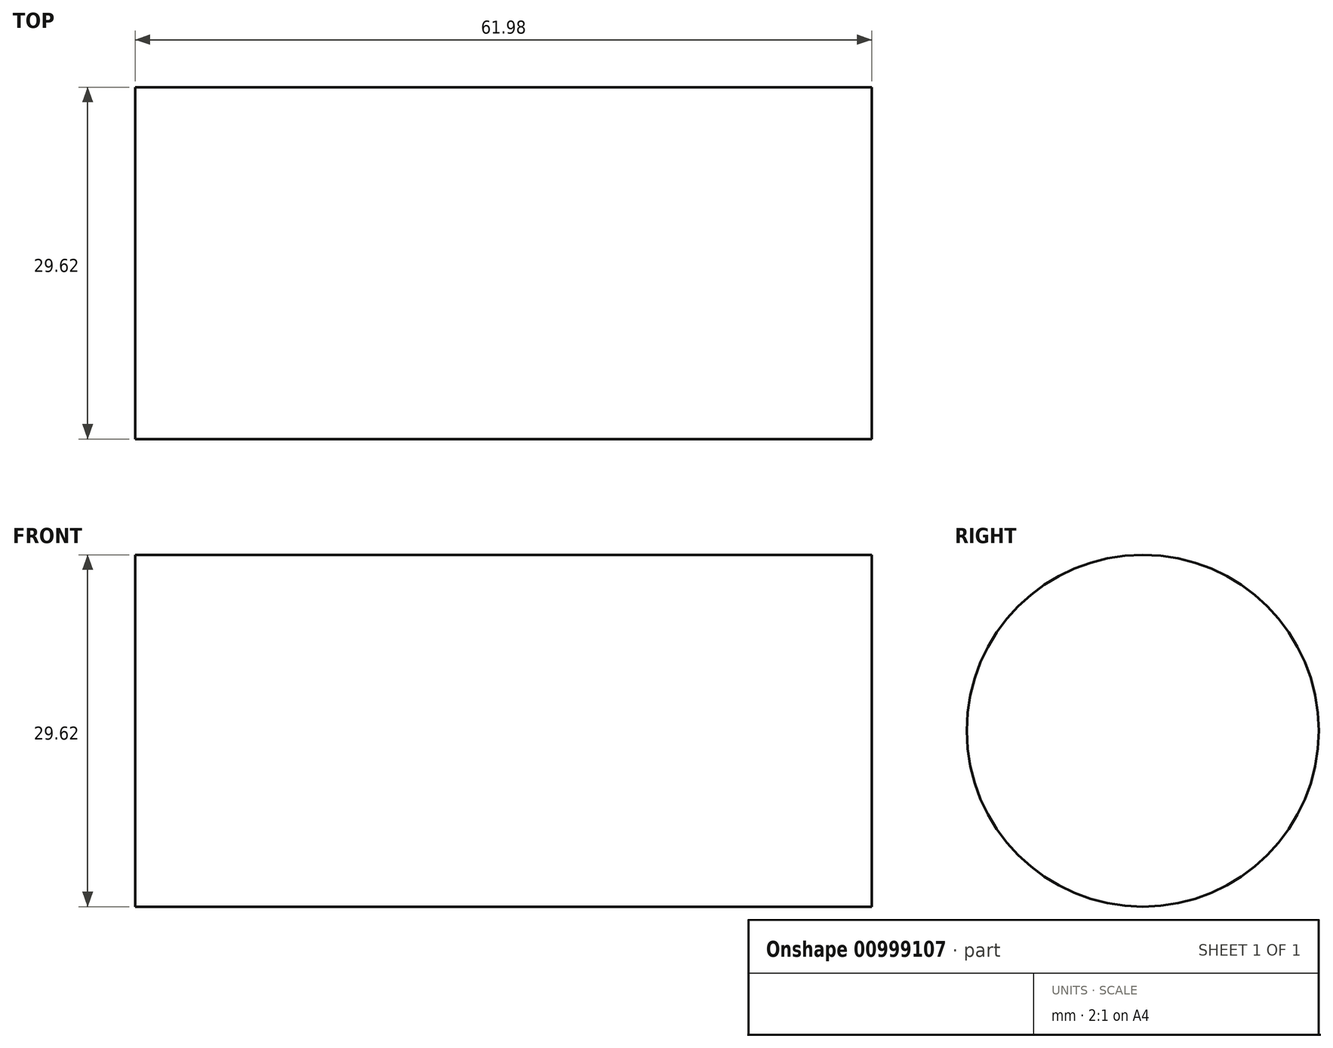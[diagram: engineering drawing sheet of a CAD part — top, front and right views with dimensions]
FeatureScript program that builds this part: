
annotation { "Feature Type Name" : "Feature", "Feature Type Description" : "" }
export const myFeature = defineFeature(function(context is Context, id is Id, definition is map)
    precondition{}
    {
        {
            var Q0;
            Q0=qCreatedBy(makeId("Top.planeOp"),FACE);
            var sketch = newSketch(context, id + "F0", { "sketchPlane" : qUnion([Q0])});
            skCircle(sketch, "E0", {"center": v(0, 0) * mm, "radius": 13.4 * mm});
            skPoint(sketch, "E0.first.point", {"position": v(-8.12, 10.66) * mm});
            skPoint(sketch, "E0.second.point", {"position": v(13.4, 0) * mm});
            skPoint(sketch, "E0.third.point", {"position": v(-2.93, -13.08) * mm});
            skSolve(sketch);
        }
        {
            var Q0;
            Q0=makeQuery(id+"F0.imprint","IMPRINT",FACE,{"disambiguationData":[TD([[makeQuery(id+"F0.imprint","IMPRINT",EDGE,{"derivedFrom":sQuery(id+"F0.wireOp",EDGE,"E0")}),1.0]])]});
            extrude(context, id + "F1", {"entities" : qUnion([Q0]), "depth" : 64.52 * mm, "offsetDistance" : 25.4 * mm});
        }
        {
            var Q0;
            Q0=makeQuery(id+"F1.opExtrude","SWEPT_BODY",BODY,{"disambiguationData":[OSD([sQuery(id+"F0.wireOp",EDGE,"E0")])]});
            deleteBodies(context, id + "F2", {"entities" : qUnion([Q0])});
        }
        {
            var Q0;
            Q0=qCreatedBy(makeId("Right.planeOp"),FACE);
            var sketch = newSketch(context, id + "F3", { "sketchPlane" : qUnion([Q0])});
            skCircle(sketch, "E1", {"center": v(-0.4, 1.18) * mm, "radius": 14.8 * mm});
            skPoint(sketch, "E1.first.point", {"position": v(8.02, 13.37) * mm});
            skPoint(sketch, "E1.second.point", {"position": v(-9.13, -10.78) * mm});
            skPoint(sketch, "E1.third.point", {"position": v(9.86, -9.5) * mm});
            skSolve(sketch);
        }
        {
            var Q0;
            Q0=makeQuery(id+"F3.imprint","IMPRINT",FACE,{"disambiguationData":[TD([[makeQuery(id+"F3.imprint","IMPRINT",EDGE,{"derivedFrom":sQuery(id+"F3.wireOp",EDGE,"E1")}),1.0]])]});
            extrude(context, id + "F4", {"entities" : qUnion([Q0]), "depth" : 61.98 * mm, "offsetDistance" : 25.4 * mm});
        }
    });
